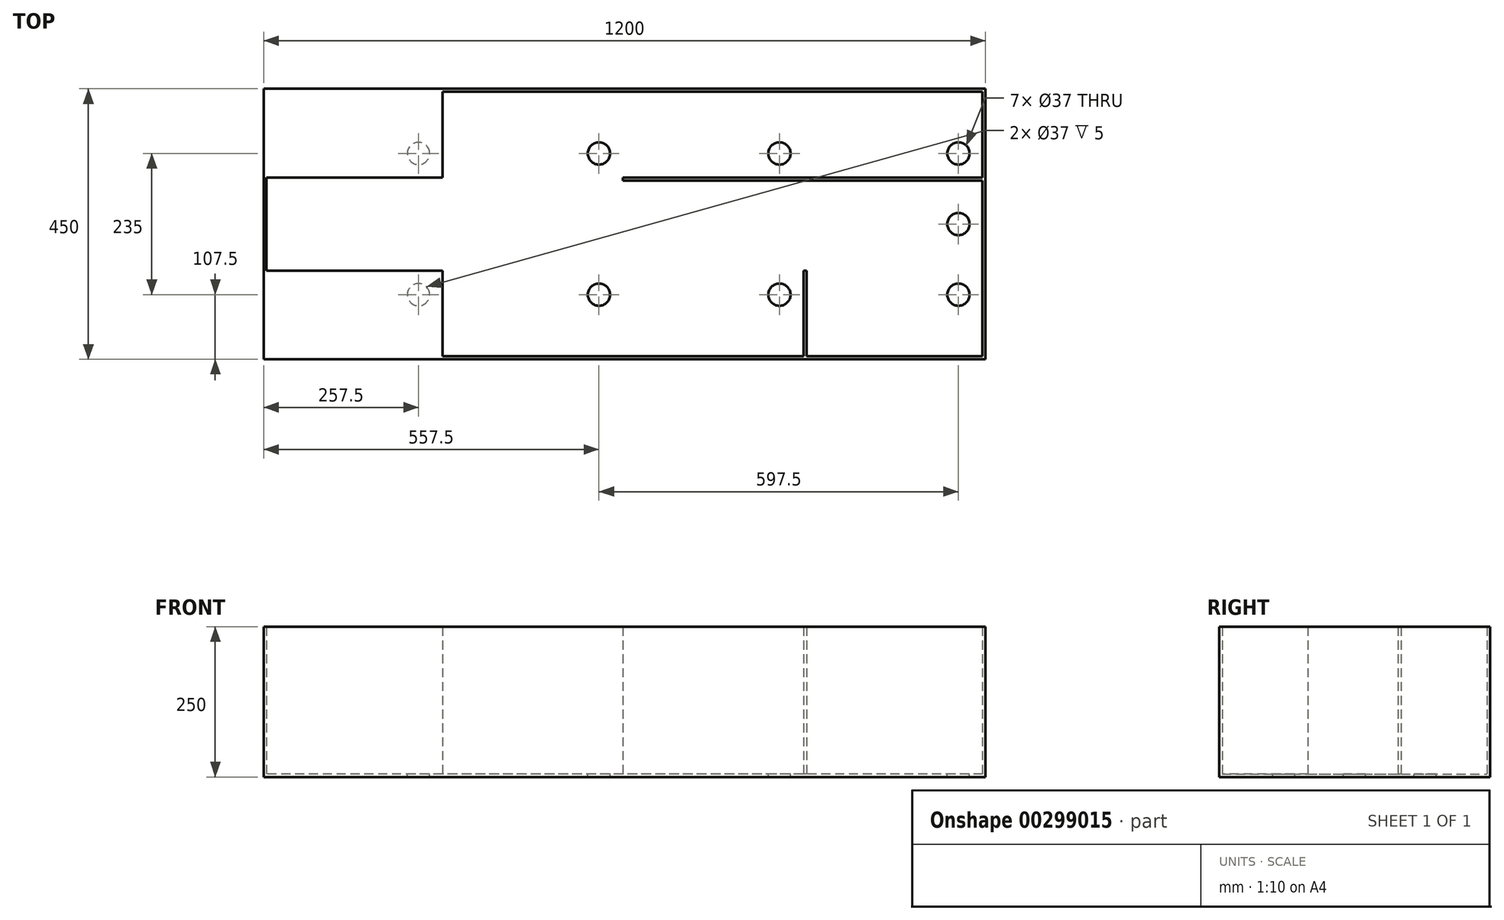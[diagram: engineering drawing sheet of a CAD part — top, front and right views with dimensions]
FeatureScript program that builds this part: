
annotation { "Feature Type Name" : "Feature", "Feature Type Description" : "" }
export const myFeature = defineFeature(function(context is Context, id is Id, definition is map)
    precondition{}
    {
        {
            var Q0;
            Q0=qCreatedBy(makeId("Top.planeOp"),FACE);
            var sketch = newSketch(context, id + "F0", { "sketchPlane" : qUnion([Q0])});
            skLineSegment(sketch, "E0.bottom", {"start": v(600, -225) * mm, "end": v(-600, -225) * mm});
            skLineSegment(sketch, "E0.top", {"start": v(600, 225) * mm, "end": v(-600, 225) * mm});
            skLineSegment(sketch, "E0.left", {"start": v(600, -225) * mm, "end": v(600, 225) * mm});
            skLineSegment(sketch, "E0.right", {"start": v(-600, -225) * mm, "end": v(-600, 225) * mm});
            skPoint(sketch, "E0.middle", {"position": v(0, 0) * mm});
            skSolve(sketch);
        }
        {
            var Q0;
            Q0=makeQuery(id+"F0.imprint","IMPRINT",FACE,{"disambiguationData":[TD([[makeQuery(id+"F0.imprint","IMPRINT",EDGE,{"derivedFrom":sQuery(id+"F0.wireOp",EDGE,"E0.bottom")}),-1.0]])]});
            extrude(context, id + "F1", {"entities" : qUnion([Q0]), "depth" : 250 * mm});
        }
        {
            var Q0;
            Q0=makeQuery(id+"F1.opExtrude","CAP_FACE",FACE,{"disambiguationData":[OSD([sQuery(id+"F0.wireOp",EDGE,"E0.bottom"),sQuery(id+"F0.wireOp",EDGE,"E0.top"),sQuery(id+"F0.wireOp",EDGE,"E0.left"),sQuery(id+"F0.wireOp",EDGE,"E0.right")])],"isStart":false});
            shell(context, id + "F2", {"entities" : qUnion([Q0]), "thickness" : 5 * mm});
        }
        {
            var Q0;
            Q0=makeQuery(id+"F2.opShell","OFFSET_FACE",FACE,{"disambiguationData":[OSD([sQuery(id+"F0.wireOp",EDGE,"E0.bottom"),sQuery(id+"F0.wireOp",EDGE,"E0.top"),sQuery(id+"F0.wireOp",EDGE,"E0.left"),sQuery(id+"F0.wireOp",EDGE,"E0.right")])]});
            var sketch = newSketch(context, id + "F3", { "sketchPlane" : qUnion([Q0])});
            skLineSegment(sketch, "E1.0", {"start": v(595, -220) * mm, "end": v(595, 220) * mm});
            skLineSegment(sketch, "E2.0", {"start": v(595, 220) * mm, "end": v(-595, 220) * mm});
            skLineSegment(sketch, "E3.0", {"start": v(595, -220) * mm, "end": v(-595, -220) * mm});
            skLineSegment(sketch, "E4.0", {"start": v(-595, -220) * mm, "end": v(-595, 220) * mm});
            skLineSegment(sketch, "E5.0", {"start": v(600, -225) * mm, "end": v(-600, -225) * mm});
            skLineSegment(sketch, "E6", {"start": v(600, -225) * mm, "end": v(600, -75) * mm});
            skLineSegment(sketch, "E7", {"start": v(600, -75) * mm, "end": v(-595, -75) * mm, "construction": true});
            skLineSegment(sketch, "E8", {"start": v(-595, -75) * mm, "end": v(-595, 75) * mm});
            skLineSegment(sketch, "E9", {"start": v(-595, 75) * mm, "end": v(595, 75) * mm, "construction": true});
            skLineSegment(sketch, "E10", {"start": v(595, -72.5) * mm, "end": v(595, -77.5) * mm});
            skPoint(sketch, "E11", {"position": v(595, -75) * mm});
            skLineSegment(sketch, "E12", {"start": v(0, 0) * mm, "end": v(595, 0) * mm, "construction": true});
            skLineSegment(sketch, "E13", {"start": v(595, -72.5) * mm, "end": v(-595, -72.5) * mm});
            skLineSegment(sketch, "E14", {"start": v(595, -77.5) * mm, "end": v(-595, -77.5) * mm});
            skLineSegment(sketch, "E15.MirrorCS", {"start": v(595, 72.5) * mm, "end": v(-595, 72.5) * mm});
            skLineSegment(sketch, "E16.MirrorCS", {"start": v(595, 77.5) * mm, "end": v(-595, 77.5) * mm});
            skLineSegment(sketch, "E17", {"start": v(600, -225) * mm, "end": v(300, -225) * mm});
            skLineSegment(sketch, "E18", {"start": v(300, -225) * mm, "end": v(0, -225) * mm});
            skLineSegment(sketch, "E19", {"start": v(0, -225) * mm, "end": v(-300, -225) * mm});
            skLineSegment(sketch, "E20", {"start": v(-300, -225) * mm, "end": v(-600, -225) * mm});
            skLineSegment(sketch, "E21", {"start": v(300, -225) * mm, "end": v(300, 220) * mm, "construction": true});
            skLineSegment(sketch, "E22", {"start": v(0, -225) * mm, "end": v(0, 220) * mm, "construction": true});
            skLineSegment(sketch, "E23", {"start": v(-300, -225) * mm, "end": v(-300, 220) * mm, "construction": true});
            skLineSegment(sketch, "E24", {"start": v(302.5, -225) * mm, "end": v(302.5, -77.5) * mm});
            skLineSegment(sketch, "E25", {"start": v(302.5, 220) * mm, "end": v(297.5, 220) * mm});
            skLineSegment(sketch, "E26", {"start": v(297.5, 220) * mm, "end": v(297.5, 77.5) * mm});
            skLineSegment(sketch, "E27", {"start": v(0, -220) * mm, "end": v(2.5, -220) * mm});
            skLineSegment(sketch, "E28", {"start": v(2.5, -220) * mm, "end": v(2.5, -77.5) * mm});
            skLineSegment(sketch, "E29", {"start": v(2.5, 220) * mm, "end": v(-2.5, 220) * mm});
            skLineSegment(sketch, "E30", {"start": v(-2.5, 220) * mm, "end": v(-2.5, 72.5) * mm});
            skLineSegment(sketch, "E31", {"start": v(-300, -220) * mm, "end": v(-297.5, -220) * mm});
            skLineSegment(sketch, "E32", {"start": v(-297.5, -220) * mm, "end": v(-297.5, -77.5) * mm});
            skLineSegment(sketch, "E33", {"start": v(-297.5, 220) * mm, "end": v(-302.5, 220) * mm});
            skLineSegment(sketch, "E34", {"start": v(-302.5, 220) * mm, "end": v(-302.5, 77.5) * mm});
            skLineSegment(sketch, "E35.trimOffspring", {"start": v(2.5, 72.5) * mm, "end": v(2.5, 220) * mm});
            skLineSegment(sketch, "E36.trimOffspring", {"start": v(302.5, 77.5) * mm, "end": v(302.5, 220) * mm});
            skLineSegment(sketch, "E37.trimOffspring", {"start": v(297.5, -77.5) * mm, "end": v(297.5, -220) * mm});
            skLineSegment(sketch, "E38.trimOffspring", {"start": v(2.5, -75) * mm, "end": v(2.5, -72.5) * mm});
            skLineSegment(sketch, "E39.trimOffspring", {"start": v(-2.5, -77.5) * mm, "end": v(-2.5, -220) * mm});
            skLineSegment(sketch, "E40.trimOffspring", {"start": v(-297.5, 77.5) * mm, "end": v(-297.5, 220) * mm});
            skLineSegment(sketch, "E41.trimOffspring", {"start": v(-302.5, -77.5) * mm, "end": v(-302.5, -220) * mm});
            skSolve(sketch);
        }
        {
            var Q0;
            {var subQ6=sQuery(id+"F3.wireOp",EDGE,"E10");Q0=makeQuery(id+"F3.imprint","IMPRINT",FACE,{"disambiguationData":[TD([[makeQuery(id+"F3.imprint","IMPRINT",EDGE,{"derivedFrom":subQ6}),1.0]])]});}
            var Q1;
            {var subQ0=sQuery(id+"F3.wireOp",EDGE,"E37.trimOffspring");Q1=makeQuery(id+"F3.imprint","IMPRINT",FACE,{"disambiguationData":[TD([[makeQuery(id+"F3.imprint","IMPRINT",EDGE,{"derivedFrom":subQ0}),1.0]])]});}
            var Q2;
            {var subQ0=sQuery(id+"F3.wireOp",EDGE,"E27");Q2=makeQuery(id+"F3.imprint","IMPRINT",FACE,{"disambiguationData":[TD([[makeQuery(id+"F3.imprint","IMPRINT",EDGE,{"derivedFrom":subQ0}),-1.0]])]});}
            var Q3;
            {var subQ1=sQuery(id+"F3.wireOp",EDGE,"E31");Q3=makeQuery(id+"F3.imprint","IMPRINT",FACE,{"disambiguationData":[TD([[makeQuery(id+"F3.imprint","IMPRINT",EDGE,{"derivedFrom":subQ1}),-1.0]])]});}
            var Q4;
            {var subQ4=sQuery(id+"F3.wireOp",EDGE,"E8");var subQ5=sQuery(id+"F3.wireOp",EDGE,"E4.0");var subQ6=makeQuery(id+"F3.imprint","INTERSECT",VERTEX,{"disambiguationData":[OD(1.0)],"derivedFrom":[subQ5,subQ4]});Q4=makeQuery(id+"F3.imprint","IMPRINT",FACE,{"disambiguationData":[TD([[makeQuery(id+"F3.imprint","IMPRINT",EDGE,{"disambiguationData":[TD([[subQ6,-1.0]])],"derivedFrom":subQ5}),-1.0]])]});}
            var Q5;
            {var subQ3=sQuery(id+"F3.wireOp",EDGE,"E1.0");var subQ5=sQuery(id+"F3.wireOp",EDGE,"E15.MirrorCS");var subQ6=makeQuery(id+"F3.imprint","INTERSECT",VERTEX,{"derivedFrom":[subQ3,subQ5]});Q5=makeQuery(id+"F3.imprint","IMPRINT",FACE,{"disambiguationData":[TD([[makeQuery(id+"F3.imprint","IMPRINT",EDGE,{"disambiguationData":[TD([[subQ6,-1.0]])],"derivedFrom":subQ3}),1.0]])]});}
            var Q6;
            {var subQ5=sQuery(id+"F3.wireOp",EDGE,"E29");Q6=makeQuery(id+"F3.imprint","IMPRINT",FACE,{"disambiguationData":[TD([[makeQuery(id+"F3.imprint","IMPRINT",EDGE,{"derivedFrom":subQ5}),1.0]])]});}
            var Q7;
            {var subQ0=sQuery(id+"F3.wireOp",EDGE,"E30");var subQ1=sQuery(id+"F3.wireOp",EDGE,"E15.MirrorCS");var subQ2=makeQuery(id+"F3.imprint","INTERSECT",VERTEX,{"derivedFrom":[subQ1,subQ0]});Q7=makeQuery(id+"F3.imprint","IMPRINT",FACE,{"disambiguationData":[TD([[makeQuery(id+"F3.imprint","IMPRINT",EDGE,{"disambiguationData":[TD([[subQ2,1.0]])],"derivedFrom":subQ1}),-1.0]])]});}
            var Q8;
            Q8=makeQuery(id+"F3.imprint","IMPRINT",FACE,{"disambiguationData":[TD([[makeQuery(id+"F3.imprint","IMPRINT",EDGE,{"derivedFrom":sQuery(id+"F3.wireOp",EDGE,"E25")}),1.0]])]});
            var Q9;
            Q9=makeQuery(id+"F3.imprint","IMPRINT",FACE,{"disambiguationData":[TD([[makeQuery(id+"F3.imprint","IMPRINT",EDGE,{"derivedFrom":sQuery(id+"F3.wireOp",EDGE,"E33")}),1.0]])]});
            var Q10;
            Q10=makeQuery(id+"F1.opExtrude","CAP_FACE",FACE,{"disambiguationData":[OSD([sQuery(id+"F0.wireOp",EDGE,"E0.bottom"),sQuery(id+"F0.wireOp",EDGE,"E0.top"),sQuery(id+"F0.wireOp",EDGE,"E0.left"),sQuery(id+"F0.wireOp",EDGE,"E0.right")])],"isStart":false});
            extrude(context, id + "F4", {"entities" : qUnion([Q0, Q1, Q2, Q3, Q4, Q5, Q6, Q7, Q8, Q9]), "operationType" : NewBodyOperationType.ADD, "endBound" : BoundingType.UP_TO_SURFACE, "endBoundEntityFace" : qUnion([Q10]), "depth" : 25 * mm});
        }
        {
            var Q0;
            {var subQ0=sQuery(id+"F0.wireOp",EDGE,"E0.left");var subQ1=sQuery(id+"F0.wireOp",EDGE,"E0.right");Q0=makeQuery(id+"F4.boolean.opBoolean","SPLIT",FACE,{"disambiguationData":[TD([makeQuery(id+"F4.opExtrude","SWEPT_FACE",FACE,{"disambiguationData":[OSD([sQuery(id+"F3.wireOp",EDGE,"E13")])]})])],"derivedFrom":makeQuery(id+"F2.opShell","OFFSET_FACE",FACE,{"disambiguationData":[OSD([sQuery(id+"F0.wireOp",EDGE,"E0.bottom"),sQuery(id+"F0.wireOp",EDGE,"E0.top"),subQ0,subQ1])]})});}
            var sketch = newSketch(context, id + "F5", { "sketchPlane" : qUnion([Q0])});
            skCircle(sketch, "E42", {"center": v(555, 0) * mm, "radius": 18.5 * mm});
            skCircle(sketch, "E43", {"center": v(555, 117.5) * mm, "radius": 18.5 * mm});
            skCircle(sketch, "E44", {"center": v(555, -117.5) * mm, "radius": 18.5 * mm});
            skCircle(sketch, "E45", {"center": v(257.5, 117.5) * mm, "radius": 18.5 * mm});
            skCircle(sketch, "E46", {"center": v(-42.5, 117.5) * mm, "radius": 18.5 * mm});
            skCircle(sketch, "E47", {"center": v(-342.5, 117.5) * mm, "radius": 18.5 * mm});
            skCircle(sketch, "E48", {"center": v(257.5, -117.5) * mm, "radius": 18.5 * mm});
            skCircle(sketch, "E49", {"center": v(-42.5, -117.5) * mm, "radius": 18.5 * mm});
            skCircle(sketch, "E50", {"center": v(-342.5, -117.5) * mm, "radius": 18.5 * mm});
            skSolve(sketch);
        }
        {
            var Q0;
            Q0=makeQuery(id+"F5.imprint","IMPRINT",FACE,{"disambiguationData":[TD([[makeQuery(id+"F5.imprint","IMPRINT",EDGE,{"derivedFrom":sQuery(id+"F5.wireOp",EDGE,"E46")}),1.0]])]});
            var Q1;
            Q1=makeQuery(id+"F5.imprint","IMPRINT",FACE,{"disambiguationData":[TD([[makeQuery(id+"F5.imprint","IMPRINT",EDGE,{"derivedFrom":sQuery(id+"F5.wireOp",EDGE,"E47")}),1.0]])]});
            var Q2;
            Q2=makeQuery(id+"F5.imprint","IMPRINT",FACE,{"disambiguationData":[TD([[makeQuery(id+"F5.imprint","IMPRINT",EDGE,{"derivedFrom":sQuery(id+"F5.wireOp",EDGE,"E50")}),1.0]])]});
            var Q3;
            Q3=makeQuery(id+"F5.imprint","IMPRINT",FACE,{"disambiguationData":[TD([[makeQuery(id+"F5.imprint","IMPRINT",EDGE,{"derivedFrom":sQuery(id+"F5.wireOp",EDGE,"E49")}),1.0]])]});
            var Q4;
            Q4=makeQuery(id+"F5.imprint","IMPRINT",FACE,{"disambiguationData":[TD([[makeQuery(id+"F5.imprint","IMPRINT",EDGE,{"derivedFrom":sQuery(id+"F5.wireOp",EDGE,"E48")}),1.0]])]});
            var Q5;
            Q5=makeQuery(id+"F5.imprint","IMPRINT",FACE,{"disambiguationData":[TD([[makeQuery(id+"F5.imprint","IMPRINT",EDGE,{"derivedFrom":sQuery(id+"F5.wireOp",EDGE,"E45")}),1.0]])]});
            var Q6;
            Q6=makeQuery(id+"F5.imprint","IMPRINT",FACE,{"disambiguationData":[TD([[makeQuery(id+"F5.imprint","IMPRINT",EDGE,{"derivedFrom":sQuery(id+"F5.wireOp",EDGE,"E43")}),1.0]])]});
            var Q7;
            Q7=makeQuery(id+"F5.imprint","IMPRINT",FACE,{"disambiguationData":[TD([[makeQuery(id+"F5.imprint","IMPRINT",EDGE,{"derivedFrom":sQuery(id+"F5.wireOp",EDGE,"E42")}),1.0]])]});
            var Q8;
            Q8=makeQuery(id+"F5.imprint","IMPRINT",FACE,{"disambiguationData":[TD([[makeQuery(id+"F5.imprint","IMPRINT",EDGE,{"derivedFrom":sQuery(id+"F5.wireOp",EDGE,"E44")}),1.0]])]});
            var Q9;
            Q9=sQuery(id+"F5.wireOp",EDGE,"E47");
            var Q10;
            Q10=sQuery(id+"F5.wireOp",EDGE,"E50");
            var Q11;
            Q11=sQuery(id+"F5.wireOp",EDGE,"E46");
            var Q12;
            Q12=sQuery(id+"F5.wireOp",EDGE,"E49");
            var Q13;
            Q13=sQuery(id+"F5.wireOp",EDGE,"E45");
            var Q14;
            Q14=sQuery(id+"F5.wireOp",EDGE,"E48");
            var Q15;
            Q15=sQuery(id+"F5.wireOp",EDGE,"E43");
            var Q16;
            Q16=sQuery(id+"F5.wireOp",EDGE,"E42");
            var Q17;
            Q17=sQuery(id+"F5.wireOp",EDGE,"E44");
            extrude(context, id + "F6", {"entities" : qUnion([Q0, Q1, Q2, Q3, Q4, Q5, Q6, Q7, Q8]), "operationType" : NewBodyOperationType.REMOVE, "surfaceEntities" : qUnion([Q9, Q10, Q11, Q12, Q13, Q14, Q15, Q16, Q17]), "oppositeDirection" : true, "depth" : 25 * mm});
        }
    });
